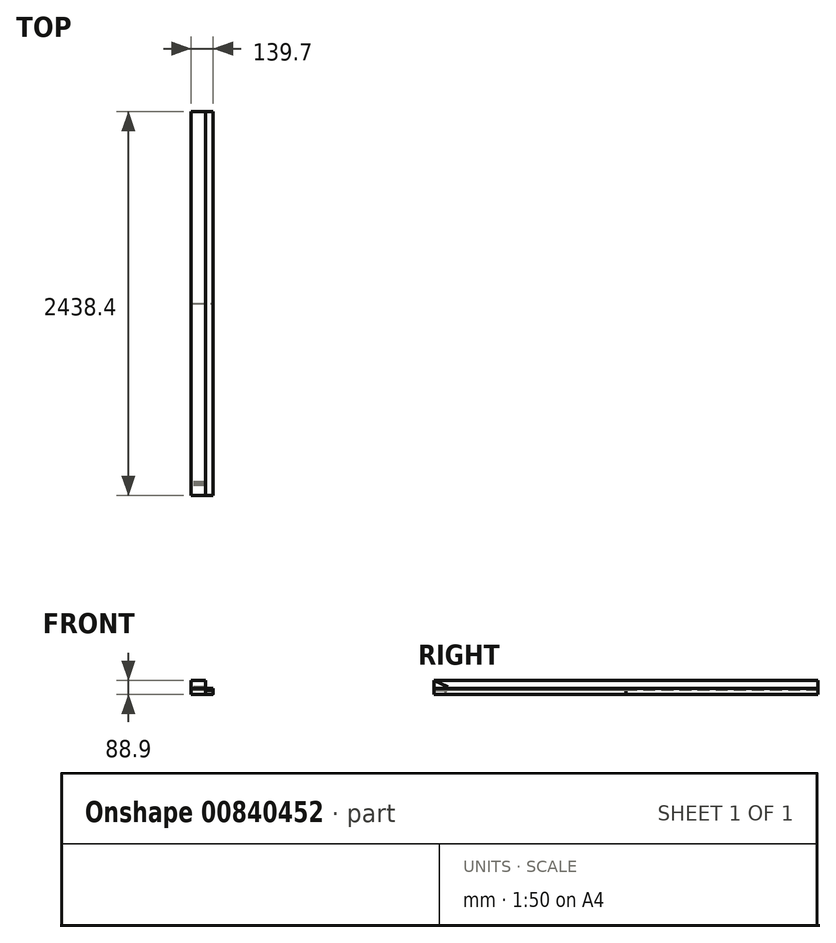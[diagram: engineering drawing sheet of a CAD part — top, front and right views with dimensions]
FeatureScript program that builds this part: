
annotation { "Feature Type Name" : "Feature", "Feature Type Description" : "" }
export const myFeature = defineFeature(function(context is Context, id is Id, definition is map)
    precondition{}
    {
        {
            var Q0;
            Q0=qCreatedBy(makeId("Front.planeOp"),FACE);
            var sketch = newSketch(context, id + "F0", { "sketchPlane" : qUnion([Q0])});
            skLineSegment(sketch, "E0", {"start": v(88.9, 88.9) * mm, "end": v(0, 88.9) * mm});
            skLineSegment(sketch, "E1", {"start": v(0, 88.9) * mm, "end": v(0, 0) * mm});
            skLineSegment(sketch, "E2", {"start": v(0, 0) * mm, "end": v(88.9, 0) * mm});
            skLineSegment(sketch, "E3", {"start": v(88.9, 0) * mm, "end": v(88.9, 88.9) * mm});
            skSolve(sketch);
        }
        {
            var Q0;
            Q0 = qSketchRegion(id + "F0", true);
            extrude(context, id + "F1", {"entities" : qUnion([Q0]), "oppositeDirection" : true, "depth" : 2438.4 * mm, "offsetDistance" : 25.4 * mm});
        }
        {
            var Q0;
            Q0=qCreatedBy(makeId("Front.planeOp"),FACE);
            var sketch = newSketch(context, id + "F2", { "sketchPlane" : qUnion([Q0])});
            skLineSegment(sketch, "E4", {"start": v(6.35, 0) * mm, "end": v(133.35, 0) * mm});
            skLineSegment(sketch, "E5", {"start": v(139.7, 6.35) * mm, "end": v(139.7, 19.05) * mm});
            skLineSegment(sketch, "E6", {"start": v(133.35, 25.4) * mm, "end": v(6.35, 25.4) * mm});
            skLineSegment(sketch, "E7", {"start": v(0, 19.05) * mm, "end": v(0, 6.35) * mm});
            skPoint(sketch, "E8.visualSharp", {"position": v(139.7, 25.4) * mm});
            skArc(sketch, "E8.filletArc", {"start": v(139.7, 19.05) * mm, "mid": v(137.84, 23.54) * mm, "end": v(133.35, 25.4) * mm});
            skPoint(sketch, "E9.visualSharp", {"position": v(0, 25.4) * mm});
            skArc(sketch, "E9.filletArc", {"start": v(6.35, 25.4) * mm, "mid": v(1.86, 23.54) * mm, "end": v(0, 19.05) * mm});
            skPoint(sketch, "E10.visualSharp", {"position": v(0, 0) * mm});
            skArc(sketch, "E10.filletArc", {"start": v(0, 6.35) * mm, "mid": v(1.86, 1.86) * mm, "end": v(6.35, 0) * mm});
            skPoint(sketch, "E11.visualSharp", {"position": v(139.7, 0) * mm});
            skArc(sketch, "E11.filletArc", {"start": v(133.35, 0) * mm, "mid": v(137.84, 1.86) * mm, "end": v(139.7, 6.35) * mm});
            skSolve(sketch);
        }
        {
            var Q0;
            Q0=makeQuery(id+"F2.imprint","IMPRINT",FACE,{"disambiguationData":[TD([[makeQuery(id+"F2.imprint","IMPRINT",EDGE,{"derivedFrom":sQuery(id+"F2.wireOp",EDGE,"E4")}),1.0]])]});
            extrude(context, id + "F3", {"entities" : qUnion([Q0]), "oppositeDirection" : true, "depth" : 1219.2 * mm, "offsetDistance" : 25.4 * mm});
        }
        {
            var Q0;
            Q0=makeQuery(id+"F2.imprint","IMPRINT",FACE,{"disambiguationData":[TD([[makeQuery(id+"F2.imprint","IMPRINT",EDGE,{"derivedFrom":sQuery(id+"F2.wireOp",EDGE,"E4")}),1.0]])]});
            extrude(context, id + "F4", {"entities" : qUnion([Q0]), "oppositeDirection" : true, "depth" : 2438.4 * mm, "offsetDistance" : 25.4 * mm});
        }
        {
            var Q0;
            Q0=qCreatedBy(makeId("Right.planeOp"),FACE);
            var sketch = newSketch(context, id + "F5", { "sketchPlane" : qUnion([Q0])});
            skLineSegment(sketch, "E12", {"start": v(0, 88.92) * mm, "end": v(86.5, 48.58) * mm});
            skLineSegment(sketch, "E13", {"start": v(86.5, 48.58) * mm, "end": v(63.85, 0) * mm});
            skLineSegment(sketch, "E14", {"start": v(63.85, 0) * mm, "end": v(0, 0) * mm});
            skLineSegment(sketch, "E15", {"start": v(0, 0) * mm, "end": v(0, 88.92) * mm});
            skSolve(sketch);
        }
        {
            var Q0;
            Q0 = qSketchRegion(id + "F5", true);
            extrude(context, id + "F6", {"entities" : qUnion([Q0]), "operationType" : NewBodyOperationType.REMOVE, "endBound" : BoundingType.UP_TO_NEXT, "depth" : 25.4 * mm, "offsetDistance" : 25.4 * mm});
        }
        {
            var Q0;
            Q0 = qSketchRegion(id + "F0", true);
            extrude(context, id + "F7", {"entities" : qUnion([Q0]), "oppositeDirection" : true, "depth" : 2438.4 * mm, "offsetDistance" : 25.4 * mm});
        }
        {
            var Q0;
            Q0=qCreatedBy(makeId("Front.planeOp"),FACE);
            var sketch = newSketch(context, id + "F8", { "sketchPlane" : qUnion([Q0])});
            skLineSegment(sketch, "E16", {"start": v(0, 0) * mm, "end": v(139.7, 0) * mm});
            skLineSegment(sketch, "E17", {"start": v(139.7, 0) * mm, "end": v(139.7, 38.1) * mm});
            skLineSegment(sketch, "E18", {"start": v(139.7, 38.1) * mm, "end": v(0, 38.1) * mm});
            skLineSegment(sketch, "E19", {"start": v(0, 38.1) * mm, "end": v(0, 0) * mm});
            skSolve(sketch);
        }
        {
            var Q0;
            Q0=makeQuery(id+"F8.imprint","IMPRINT",FACE,{"disambiguationData":[TD([[makeQuery(id+"F8.imprint","IMPRINT",EDGE,{"derivedFrom":sQuery(id+"F8.wireOp",EDGE,"E16")}),1.0]])]});
            extrude(context, id + "F9", {"entities" : qUnion([Q0]), "oppositeDirection" : true, "depth" : 2438.4 * mm, "offsetDistance" : 25.4 * mm});
        }
    });
